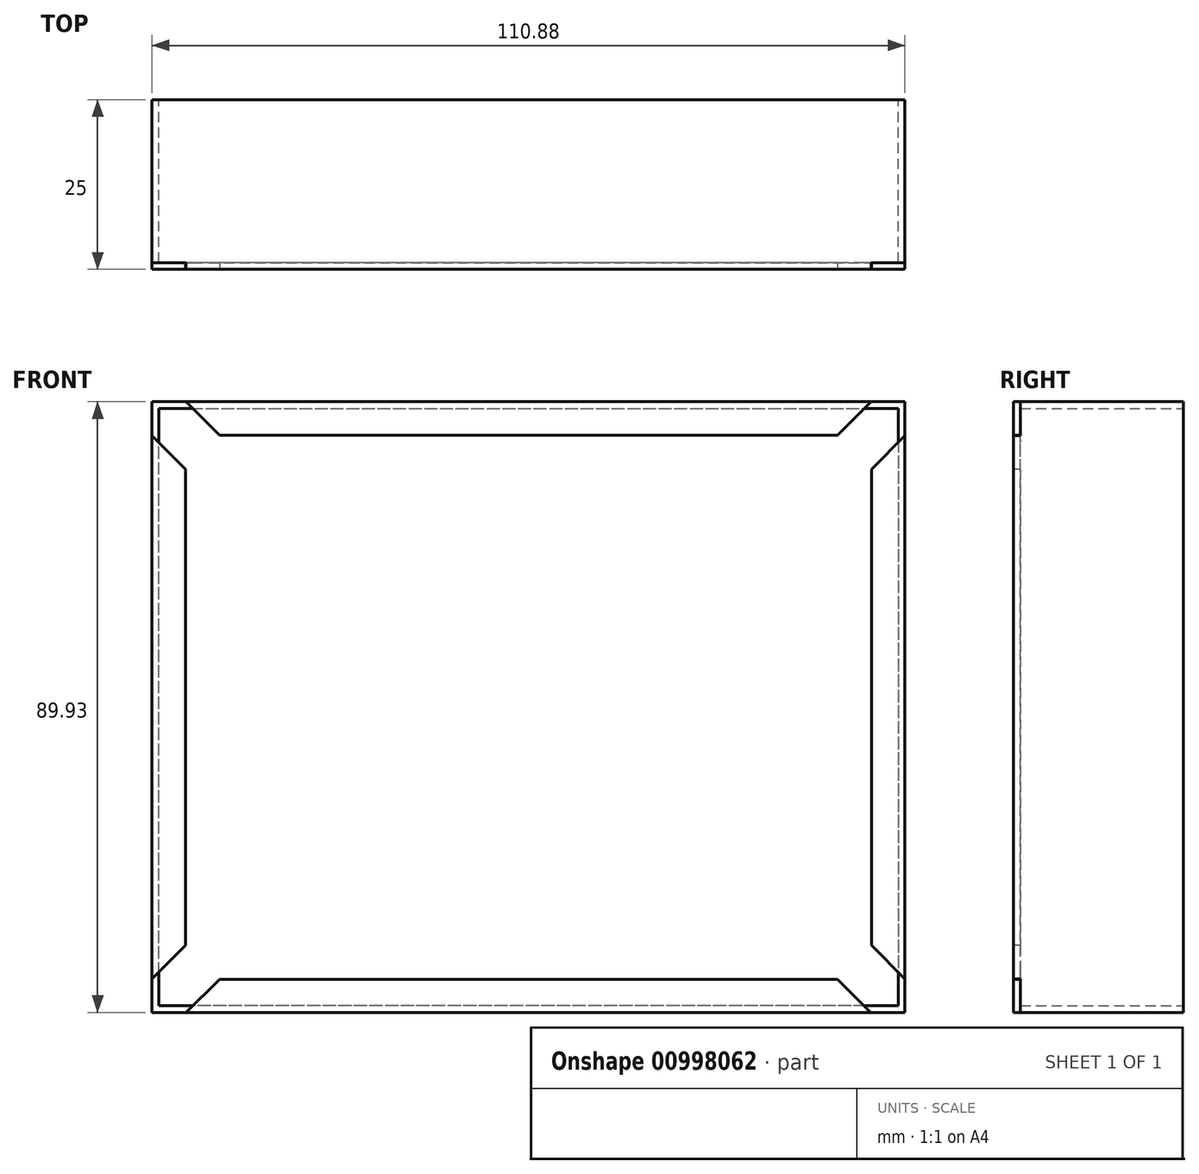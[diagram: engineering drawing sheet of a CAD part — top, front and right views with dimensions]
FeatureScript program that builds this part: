
annotation { "Feature Type Name" : "Feature", "Feature Type Description" : "" }
export const myFeature = defineFeature(function(context is Context, id is Id, definition is map)
    precondition{}
    {
        {
            var Q0;
            Q0=qCreatedBy(makeId("Front.planeOp"),FACE);
            var sketch = newSketch(context, id + "F0", { "sketchPlane" : qUnion([Q0])});
            skLineSegment(sketch, "E0", {"start": v(0, 38.44) * mm, "end": v(-3.5, 38.44) * mm, "construction": true});
            skLineSegment(sketch, "E1", {"start": v(-3.5, 38.44) * mm, "end": v(-3.5, 45) * mm, "construction": true});
            skLineSegment(sketch, "E2", {"start": v(0, 38.44) * mm, "end": v(3.5, 38.44) * mm, "construction": true});
            skLineSegment(sketch, "E3", {"start": v(-55.44, 3.5) * mm, "end": v(-48.44, 3.5) * mm, "construction": true});
            skLineSegment(sketch, "E4", {"start": v(-48.44, 3.5) * mm, "end": v(-48.44, -3.5) * mm, "construction": true});
            skLineSegment(sketch, "E5", {"start": v(-48.44, -3.5) * mm, "end": v(-55.44, -3.5) * mm, "construction": true});
            skLineSegment(sketch, "E6", {"start": v(-55.44, 3.5) * mm, "end": v(-55.44, 40) * mm});
            skLineSegment(sketch, "E7", {"start": v(-55.44, -3.5) * mm, "end": v(-55.44, -39.93) * mm});
            skLineSegment(sketch, "E8", {"start": v(0, 38.44) * mm, "end": v(0, -16.53) * mm, "construction": true});
            skLineSegment(sketch, "E9", {"start": v(42.56, 0) * mm, "end": v(-13.66, 0) * mm, "construction": true});
            skLineSegment(sketch, "E10", {"start": v(0, 0) * mm, "end": v(-4.78, 0) * mm, "construction": true});
            skLineSegment(sketch, "E11", {"start": v(-50.44, -44.93) * mm, "end": v(-3.5, -44.93) * mm});
            skLineSegment(sketch, "E12", {"start": v(-3.5, -44.93) * mm, "end": v(-3.5, -37.93) * mm, "construction": true});
            skLineSegment(sketch, "E13", {"start": v(-3.5, -37.93) * mm, "end": v(3.5, -37.93) * mm, "construction": true});
            skLineSegment(sketch, "E14", {"start": v(-3.5, 45) * mm, "end": v(-50.44, 45) * mm});
            skLineSegment(sketch, "E15.MirrorCS", {"start": v(50.44, -44.93) * mm, "end": v(3.5, -44.93) * mm});
            skLineSegment(sketch, "E16.MirrorCS", {"start": v(55.44, -3.5) * mm, "end": v(55.44, -39.93) * mm});
            skLineSegment(sketch, "E17.MirrorCS", {"start": v(55.44, 3.5) * mm, "end": v(55.44, 40) * mm});
            skLineSegment(sketch, "E18.MirrorCS", {"start": v(3.5, 45) * mm, "end": v(50.44, 45) * mm});
            skLineSegment(sketch, "E19", {"start": v(3.5, 45) * mm, "end": v(3.5, 38.44) * mm, "construction": true});
            skLineSegment(sketch, "E20", {"start": v(3.5, -37.93) * mm, "end": v(3.5, -44.93) * mm, "construction": true});
            skLineSegment(sketch, "E21.MirrorCS", {"start": v(55.44, 3.5) * mm, "end": v(48.44, 3.5) * mm, "construction": true});
            skLineSegment(sketch, "E22.MirrorCS", {"start": v(48.44, -3.5) * mm, "end": v(55.44, -3.5) * mm, "construction": true});
            skLineSegment(sketch, "E23.MirrorCS", {"start": v(48.44, 3.5) * mm, "end": v(48.44, -3.5) * mm, "construction": true});
            skLineSegment(sketch, "E24", {"start": v(-55.44, 3.5) * mm, "end": v(-55.44, -3.5) * mm});
            skLineSegment(sketch, "E25", {"start": v(-50.49, 35.05) * mm, "end": v(-55.44, 40) * mm});
            skLineSegment(sketch, "E26", {"start": v(-50.44, 45) * mm, "end": v(-45.44, 45) * mm});
            skLineSegment(sketch, "E27", {"start": v(-3.5, 45) * mm, "end": v(3.5, 45) * mm});
            skLineSegment(sketch, "E28", {"start": v(55.44, 3.5) * mm, "end": v(55.44, -3.5) * mm});
            skLineSegment(sketch, "E29", {"start": v(3.5, -44.93) * mm, "end": v(-3.5, -44.93) * mm});
            skLineSegment(sketch, "E30", {"start": v(-50.44, 45) * mm, "end": v(-45.49, 40.05) * mm});
            skLineSegment(sketch, "E31", {"start": v(-50.49, 35.05) * mm, "end": v(-45.49, 40.05) * mm, "construction": true});
            skLineSegment(sketch, "E32.MirrorCS", {"start": v(-50.49, -35.05) * mm, "end": v(-55.44, -40) * mm});
            skLineSegment(sketch, "E33.MirrorCS", {"start": v(-50.49, -35.05) * mm, "end": v(-45.49, -40.05) * mm, "construction": true});
            skLineSegment(sketch, "E34.MirrorCS", {"start": v(50.44, 45) * mm, "end": v(45.49, 40.05) * mm});
            skLineSegment(sketch, "E35.MirrorCS", {"start": v(50.49, 35.05) * mm, "end": v(45.49, 40.05) * mm, "construction": true});
            skLineSegment(sketch, "E36.MirrorCS", {"start": v(50.49, 35.05) * mm, "end": v(55.44, 40) * mm});
            skLineSegment(sketch, "E37.MirrorCS", {"start": v(50.49, -35.05) * mm, "end": v(55.44, -40) * mm});
            skLineSegment(sketch, "E38.MirrorCS", {"start": v(50.49, -35.05) * mm, "end": v(45.49, -40.05) * mm, "construction": true});
            skLineSegment(sketch, "E39.MirrorCS", {"start": v(50.44, -45) * mm, "end": v(45.49, -40.05) * mm});
            skLineSegment(sketch, "E40", {"start": v(-55.44, 40) * mm, "end": v(-55.44, 45) * mm});
            skLineSegment(sketch, "E41", {"start": v(-55.44, 45) * mm, "end": v(-50.44, 45) * mm});
            skLineSegment(sketch, "E42", {"start": v(55.44, 40) * mm, "end": v(55.44, 45) * mm});
            skLineSegment(sketch, "E43", {"start": v(55.44, 45) * mm, "end": v(50.44, 45) * mm});
            skLineSegment(sketch, "E44", {"start": v(55.44, -39.93) * mm, "end": v(55.44, -44.93) * mm});
            skLineSegment(sketch, "E45", {"start": v(55.44, -44.93) * mm, "end": v(50.44, -44.93) * mm});
            skLineSegment(sketch, "E46", {"start": v(-55.44, -40) * mm, "end": v(-55.44, -44.93) * mm});
            skLineSegment(sketch, "E47", {"start": v(-55.44, -44.93) * mm, "end": v(-50.44, -44.93) * mm});
            skLineSegment(sketch, "E48", {"start": v(-55.44, -39.93) * mm, "end": v(-55.44, -40) * mm});
            skLineSegment(sketch, "E49", {"start": v(-45.49, -40.05) * mm, "end": v(-50.44, -44.93) * mm});
            skLineSegment(sketch, "E50", {"start": v(45.49, 40.05) * mm, "end": v(-45.49, 40.05) * mm});
            skLineSegment(sketch, "E51", {"start": v(45.49, -40.05) * mm, "end": v(-45.49, -40.05) * mm});
            skLineSegment(sketch, "E52", {"start": v(-50.49, 35.05) * mm, "end": v(-50.49, -35.05) * mm});
            skLineSegment(sketch, "E53", {"start": v(50.49, 35.05) * mm, "end": v(50.49, -35.05) * mm});
            skSolve(sketch);
        }
        {
            var Q0;
            Q0=makeQuery(id+"F0.imprint","IMPRINT",FACE,{"disambiguationData":[TD([[makeQuery(id+"F0.imprint","IMPRINT",EDGE,{"derivedFrom":sQuery(id+"F0.wireOp",EDGE,"E14")}),1.0]])]});
            var Q1;
            Q1=makeQuery(id+"F0.imprint","IMPRINT",FACE,{"disambiguationData":[TD([[makeQuery(id+"F0.imprint","IMPRINT",EDGE,{"derivedFrom":sQuery(id+"F0.wireOp",EDGE,"E25")}),-1.0]])]});
            var Q2;
            {var subQ0=sQuery(id+"F0.wireOp",EDGE,"E16.MirrorCS");Q2=makeQuery(id+"F0.imprint","IMPRINT",FACE,{"disambiguationData":[TD([[makeQuery(id+"F0.imprint","IMPRINT",EDGE,{"derivedFrom":subQ0}),-1.0]])]});}
            var Q3;
            Q3=makeQuery(id+"F0.imprint","IMPRINT",FACE,{"disambiguationData":[TD([[makeQuery(id+"F0.imprint","IMPRINT",EDGE,{"derivedFrom":sQuery(id+"F0.wireOp",EDGE,"E11")}),1.0]])]});
            var Q4;
            Q4=makeQuery(id+"F0.imprint","IMPRINT",FACE,{"disambiguationData":[TD([[makeQuery(id+"F0.imprint","IMPRINT",EDGE,{"derivedFrom":sQuery(id+"F0.wireOp",EDGE,"E6")}),-1.0]])]});
            extrude(context, id + "F1", {"entities" : qUnion([Q0, Q1, Q2, Q3, Q4]), "oppositeDirection" : true, "depth" : 25 * mm, "offsetDistance" : 25 * mm});
        }
        {
            var Q0;
            Q0=makeQuery(id+"F0.imprint","IMPRINT",FACE,{"disambiguationData":[TD([[makeQuery(id+"F0.imprint","IMPRINT",EDGE,{"derivedFrom":sQuery(id+"F0.wireOp",EDGE,"E25")}),-1.0]])]});
            extrude(context, id + "F2", {"entities" : qUnion([Q0]), "operationType" : NewBodyOperationType.REMOVE, "oppositeDirection" : true, "depth" : 1 * mm, "offsetDistance" : 25 * mm});
        }
        {
            var Q0;
            Q0=makeQuery(id+"F1.opExtrude","CAP_FACE",FACE,{"disambiguationData":[OSD([sQuery(id+"F0.wireOp",EDGE,"E6"),sQuery(id+"F0.wireOp",EDGE,"E7"),sQuery(id+"F0.wireOp",EDGE,"E11"),sQuery(id+"F0.wireOp",EDGE,"E14"),sQuery(id+"F0.wireOp",EDGE,"E15.MirrorCS"),sQuery(id+"F0.wireOp",EDGE,"E16.MirrorCS"),sQuery(id+"F0.wireOp",EDGE,"E17.MirrorCS"),sQuery(id+"F0.wireOp",EDGE,"E18.MirrorCS"),sQuery(id+"F0.wireOp",EDGE,"E24"),sQuery(id+"F0.wireOp",EDGE,"E26"),sQuery(id+"F0.wireOp",EDGE,"E27"),sQuery(id+"F0.wireOp",EDGE,"E28"),sQuery(id+"F0.wireOp",EDGE,"E29"),sQuery(id+"F0.wireOp",EDGE,"E40"),sQuery(id+"F0.wireOp",EDGE,"E41"),sQuery(id+"F0.wireOp",EDGE,"E42"),sQuery(id+"F0.wireOp",EDGE,"E43"),sQuery(id+"F0.wireOp",EDGE,"E44"),sQuery(id+"F0.wireOp",EDGE,"E45"),sQuery(id+"F0.wireOp",EDGE,"E46"),sQuery(id+"F0.wireOp",EDGE,"E47"),sQuery(id+"F0.wireOp",EDGE,"E48")])],"isStart":false});
            var sketch = newSketch(context, id + "F3", { "sketchPlane" : qUnion([Q0])});
            skLineSegment(sketch, "E54.0.0", {"start": v(-55.44, 45) * mm, "end": v(-55.44, -44.93) * mm, "construction": true});
            skLineSegment(sketch, "E54.0.1", {"start": v(-55.44, -44.93) * mm, "end": v(55.44, -44.93) * mm, "construction": true});
            skLineSegment(sketch, "E54.0.2", {"start": v(55.44, -44.93) * mm, "end": v(55.44, 45) * mm, "construction": true});
            skLineSegment(sketch, "E54.0.3", {"start": v(55.44, 45) * mm, "end": v(-55.44, 45) * mm, "construction": true});
            skLineSegment(sketch, "E55.0", {"start": v(54.44, 44) * mm, "end": v(-54.44, 44) * mm});
            skLineSegment(sketch, "E55.1", {"start": v(54.44, -43.93) * mm, "end": v(54.44, 44) * mm});
            skLineSegment(sketch, "E55.2", {"start": v(-54.44, -43.93) * mm, "end": v(54.44, -43.93) * mm});
            skLineSegment(sketch, "E55.3", {"start": v(-54.44, 44) * mm, "end": v(-54.44, -43.93) * mm});
            skSolve(sketch);
        }
        {
            var Q0;
            Q0=makeQuery(id+"F3.imprint","IMPRINT",FACE,{"disambiguationData":[TD([[makeQuery(id+"F3.imprint","IMPRINT",EDGE,{"derivedFrom":sQuery(id+"F3.wireOp",EDGE,"E55.0")}),1.0]])]});
            extrude(context, id + "F4", {"entities" : qUnion([Q0]), "operationType" : NewBodyOperationType.REMOVE, "oppositeDirection" : true, "depth" : 24 * mm, "offsetDistance" : 25 * mm});
        }
    });
